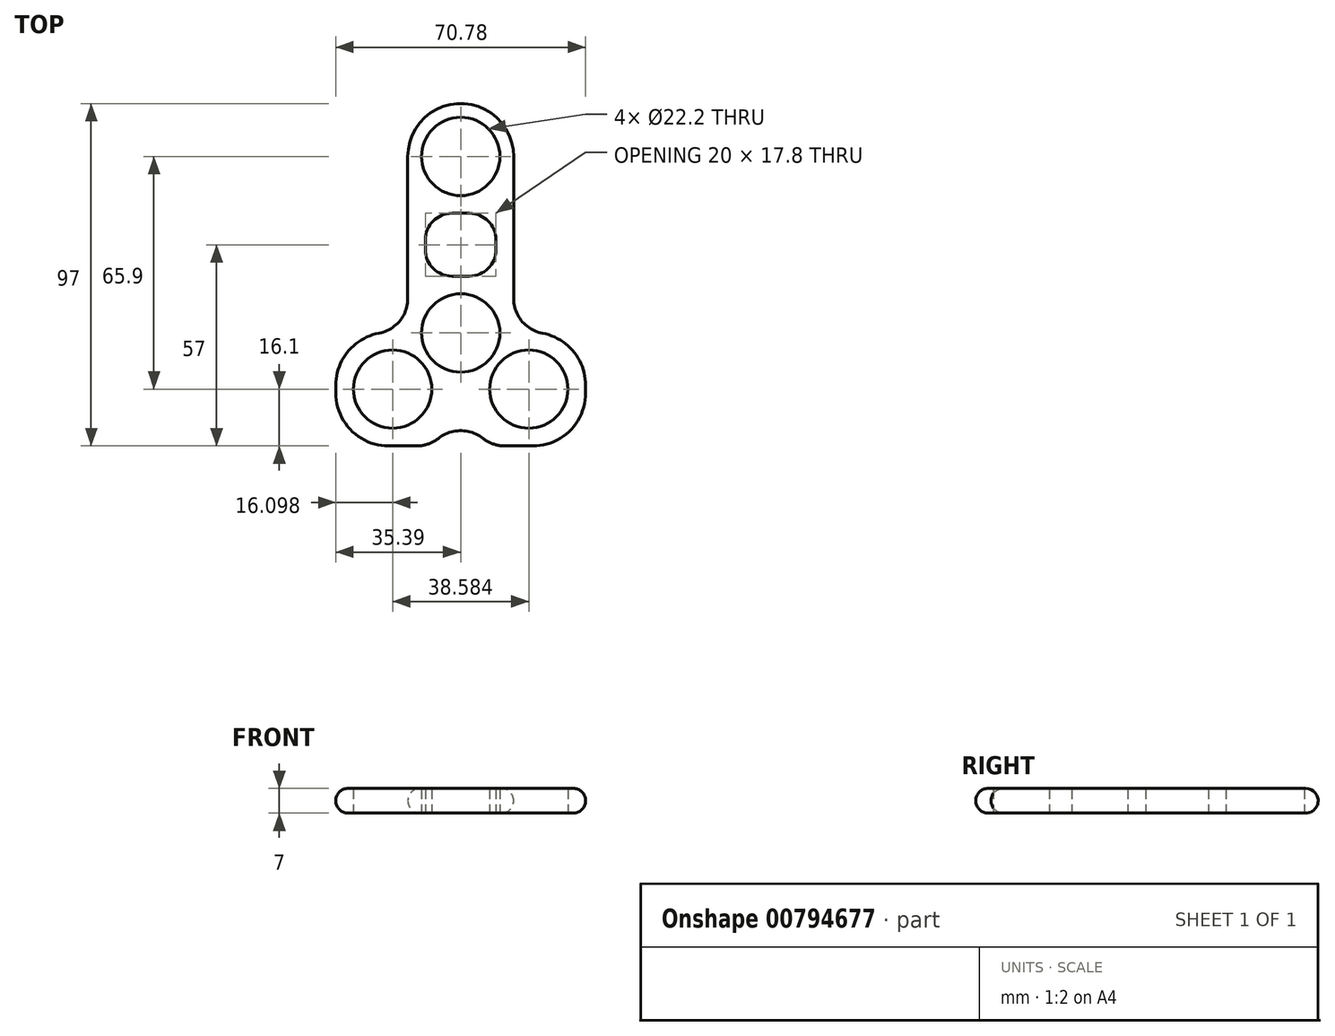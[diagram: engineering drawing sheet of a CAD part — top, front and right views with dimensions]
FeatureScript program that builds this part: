
annotation { "Feature Type Name" : "Feature", "Feature Type Description" : "" }
export const myFeature = defineFeature(function(context is Context, id is Id, definition is map)
    precondition{}
    {
        {
            var Q0;
            Q0=qCreatedBy(makeId("Top.planeOp"),FACE);
            var sketch = newSketch(context, id + "F0", { "sketchPlane" : qUnion([Q0])});
            skCircle(sketch, "E0", {"center": v(0, 50) * mm, "radius": 11.1 * mm});
            skCircle(sketch, "E1", {"center": v(0, 0) * mm, "radius": 11.1 * mm});
            skCircle(sketch, "E2", {"center": v(-19.3, -15.9) * mm, "radius": 11.1 * mm});
            skCircle(sketch, "E3", {"center": v(19.3, -15.9) * mm, "radius": 11.1 * mm});
            skLineSegment(sketch, "E4", {"start": v(-15, 0.2) * mm, "end": v(-15, 60.2) * mm});
            skLineSegment(sketch, "E5", {"start": v(-15, 0.2) * mm, "end": v(-35.4, 0.2) * mm});
            skLineSegment(sketch, "E6", {"start": v(-35.4, 0.2) * mm, "end": v(-35.4, -32) * mm});
            skLineSegment(sketch, "E7", {"start": v(-35.4, -32) * mm, "end": v(0, -32) * mm});
            skLineSegment(sketch, "E8", {"start": v(0, -32) * mm, "end": v(35.4, -32) * mm});
            skLineSegment(sketch, "E9", {"start": v(35.4, -32) * mm, "end": v(35.4, 0.2) * mm});
            skLineSegment(sketch, "E10", {"start": v(35.4, 0.2) * mm, "end": v(15, 0.2) * mm});
            skLineSegment(sketch, "E11", {"start": v(15, 0.2) * mm, "end": v(15, 60.2) * mm});
            skLineSegment(sketch, "E12", {"start": v(15, 60.2) * mm, "end": v(-15, 60.2) * mm});
            skLineSegment(sketch, "E13", {"start": v(-65.85, -15.9) * mm, "end": v(63.66, -15.9) * mm, "construction": true});
            skCircle(sketch, "E14", {"center": v(0, 50) * mm, "radius": 15 * mm});
            skArc(sketch, "E15", {"start": v(8.4, -32) * mm, "mid": v(0, -27.7) * mm, "end": v(-8.4, -32) * mm});
            skLineSegment(sketch, "E16", {"start": v(-10, 33.9) * mm, "end": v(-10, 16.1) * mm});
            skLineSegment(sketch, "E17", {"start": v(-10, 16.1) * mm, "end": v(10, 16.1) * mm});
            skLineSegment(sketch, "E18", {"start": v(10, 16.1) * mm, "end": v(10, 33.9) * mm});
            skLineSegment(sketch, "E19", {"start": v(10, 33.9) * mm, "end": v(-10, 33.9) * mm});
            skSolve(sketch);
        }
        {
            var Q0;
            {var subQ0=sQuery(id+"F0.wireOp",EDGE,"E14");var subQ1=sQuery(id+"F0.wireOp",EDGE,"E12");var subQ2=makeQuery(id+"F0.imprint","INTERSECT",VERTEX,{"disambiguationData":[OD(0.0)],"derivedFrom":[subQ1,subQ0]});Q0=makeQuery(id+"F0.imprint","IMPRINT",FACE,{"disambiguationData":[TD([[makeQuery(id+"F0.imprint","IMPRINT",EDGE,{"disambiguationData":[TD([[subQ2,-1.0]])],"derivedFrom":subQ1}),-1.0]])]});}
            var Q1;
            Q1=makeQuery(id+"F0.imprint","IMPRINT",FACE,{"disambiguationData":[TD([[makeQuery(id+"F0.imprint","IMPRINT",EDGE,{"derivedFrom":sQuery(id+"F0.wireOp",EDGE,"E1")}),-1.0]])]});
            var Q2;
            Q2=makeQuery(id+"F0.imprint","IMPRINT",FACE,{"disambiguationData":[TD([[makeQuery(id+"F0.imprint","IMPRINT",EDGE,{"derivedFrom":sQuery(id+"F0.wireOp",EDGE,"E0")}),-1.0]])]});
            var Q3;
            {var subQ2=sQuery(id+"F0.wireOp",EDGE,"E12");var subQ5=sQuery(id+"F0.wireOp",EDGE,"E0");var subQ7=makeQuery(id+"F0.imprint","INTERSECT",VERTEX,{"disambiguationData":[OD(0.0)],"derivedFrom":[subQ5,subQ2]});Q3=makeQuery(id+"F0.imprint","IMPRINT",FACE,{"disambiguationData":[TD([[makeQuery(id+"F0.imprint","IMPRINT",EDGE,{"disambiguationData":[TD([[subQ7,1.0]])],"derivedFrom":subQ5}),-1.0]])]});}
            extrude(context, id + "F1", {"entities" : qUnion([Q0, Q1, Q2, Q3]), "depth" : 7 * mm, "offsetDistance" : 25 * mm});
        }
        {
            var Q0;
            Q0=makeQuery(id+"F1.opExtrude","SWEPT_EDGE",EDGE,{"disambiguationData":[OSD([sQuery(id+"F0.wireOp",EDGE,"E5"),sQuery(id+"F0.wireOp",EDGE,"E6")])]});
            var Q1;
            Q1=makeQuery(id+"F1.opExtrude","SWEPT_EDGE",EDGE,{"disambiguationData":[OSD([sQuery(id+"F0.wireOp",EDGE,"E6"),sQuery(id+"F0.wireOp",EDGE,"E7")])]});
            var Q2;
            Q2=makeQuery(id+"F1.opExtrude","SWEPT_EDGE",EDGE,{"disambiguationData":[OSD([sQuery(id+"F0.wireOp",EDGE,"E9"),sQuery(id+"F0.wireOp",EDGE,"E10")])]});
            var Q3;
            Q3=makeQuery(id+"F1.opExtrude","SWEPT_EDGE",EDGE,{"disambiguationData":[OSD([sQuery(id+"F0.wireOp",EDGE,"E8"),sQuery(id+"F0.wireOp",EDGE,"E9")])]});
            fillet(context, id + "F2", {"entities" : qUnion([Q0, Q1, Q2, Q3]), "radius" : 15 * mm, "tangentPropagation" : true, "allowEdgeOverflow" : false});
        }
        {
            var Q0;
            Q0=makeQuery(id+"F1.opExtrude","SWEPT_EDGE",EDGE,{"disambiguationData":[OSD([sQuery(id+"F0.wireOp",EDGE,"E7"),sQuery(id+"F0.wireOp",EDGE,"5uxY0wwV-qU5a-CC5X-hWH9-kk7bbz8uba4x")])]});
            var Q1;
            Q1=makeQuery(id+"F1.opExtrude","SWEPT_EDGE",EDGE,{"disambiguationData":[OSD([sQuery(id+"F0.wireOp",EDGE,"E8"),sQuery(id+"F0.wireOp",EDGE,"5uxY0wwV-qU5a-CC5X-hWH9-kk7bbz8uba4x")])]});
            var Q2;
            Q2=makeQuery(id+"F1.opExtrude","SWEPT_EDGE",EDGE,{"disambiguationData":[OSD([sQuery(id+"F0.wireOp",EDGE,"E10"),sQuery(id+"F0.wireOp",EDGE,"E11")])]});
            var Q3;
            Q3=makeQuery(id+"F1.opExtrude","SWEPT_EDGE",EDGE,{"disambiguationData":[OSD([sQuery(id+"F0.wireOp",EDGE,"E4"),sQuery(id+"F0.wireOp",EDGE,"E5")])]});
            fillet(context, id + "F3", {"entities" : qUnion([Q0, Q1, Q2, Q3]), "radius" : 10 * mm, "tangentPropagation" : true, "allowEdgeOverflow" : false});
        }
        {
            var Q0;
            {var subQ0=sQuery(id+"F0.wireOp",EDGE,"E7");var subQ1=sQuery(id+"F0.wireOp",EDGE,"E6");Q0=makeQuery(id+"F2.opFillet","BLEND_EDGE",EDGE,{"blendedFrom":[makeQuery(id+"F1.opExtrude","SWEPT_EDGE",EDGE,{"disambiguationData":[OSD([subQ1,subQ0])]}),makeQuery(id+"F1.opExtrude","CAP_FACE",FACE,{"disambiguationData":[OSD([sQuery(id+"F0.wireOp",EDGE,"E0"),sQuery(id+"F0.wireOp",EDGE,"E1"),sQuery(id+"F0.wireOp",EDGE,"E2"),sQuery(id+"F0.wireOp",EDGE,"E3"),sQuery(id+"F0.wireOp",EDGE,"E4"),sQuery(id+"F0.wireOp",EDGE,"E5"),subQ1,subQ0,sQuery(id+"F0.wireOp",EDGE,"E8"),sQuery(id+"F0.wireOp",EDGE,"E9"),sQuery(id+"F0.wireOp",EDGE,"E10"),sQuery(id+"F0.wireOp",EDGE,"E11"),sQuery(id+"F0.wireOp",EDGE,"E14"),sQuery(id+"F0.wireOp",EDGE,"5uxY0wwV-qU5a-CC5X-hWH9-kk7bbz8uba4x")])],"isStart":false})],"blendedInto":[makeQuery(id+"F1.opExtrude","CAP_FACE",FACE,{"disambiguationData":[OSD([sQuery(id+"F0.wireOp",EDGE,"E0"),sQuery(id+"F0.wireOp",EDGE,"E1"),sQuery(id+"F0.wireOp",EDGE,"E2"),sQuery(id+"F0.wireOp",EDGE,"E3"),sQuery(id+"F0.wireOp",EDGE,"E4"),sQuery(id+"F0.wireOp",EDGE,"E5"),subQ1,subQ0,sQuery(id+"F0.wireOp",EDGE,"E8"),sQuery(id+"F0.wireOp",EDGE,"E9"),sQuery(id+"F0.wireOp",EDGE,"E10"),sQuery(id+"F0.wireOp",EDGE,"E11"),sQuery(id+"F0.wireOp",EDGE,"E14"),sQuery(id+"F0.wireOp",EDGE,"5uxY0wwV-qU5a-CC5X-hWH9-kk7bbz8uba4x")])],"isStart":false})]});}
            var Q1;
            {var subQ0=sQuery(id+"F0.wireOp",EDGE,"E9");var subQ1=sQuery(id+"F0.wireOp",EDGE,"E8");Q1=makeQuery(id+"F2.opFillet","BLEND_EDGE",EDGE,{"blendedFrom":[makeQuery(id+"F1.opExtrude","SWEPT_EDGE",EDGE,{"disambiguationData":[OSD([subQ1,subQ0])]}),makeQuery(id+"F1.opExtrude","CAP_FACE",FACE,{"disambiguationData":[OSD([sQuery(id+"F0.wireOp",EDGE,"E0"),sQuery(id+"F0.wireOp",EDGE,"E1"),sQuery(id+"F0.wireOp",EDGE,"E2"),sQuery(id+"F0.wireOp",EDGE,"E3"),sQuery(id+"F0.wireOp",EDGE,"E4"),sQuery(id+"F0.wireOp",EDGE,"E5"),sQuery(id+"F0.wireOp",EDGE,"E6"),sQuery(id+"F0.wireOp",EDGE,"E7"),subQ1,subQ0,sQuery(id+"F0.wireOp",EDGE,"E10"),sQuery(id+"F0.wireOp",EDGE,"E11"),sQuery(id+"F0.wireOp",EDGE,"E14"),sQuery(id+"F0.wireOp",EDGE,"5uxY0wwV-qU5a-CC5X-hWH9-kk7bbz8uba4x")])],"isStart":true})],"blendedInto":[makeQuery(id+"F1.opExtrude","CAP_FACE",FACE,{"disambiguationData":[OSD([sQuery(id+"F0.wireOp",EDGE,"E0"),sQuery(id+"F0.wireOp",EDGE,"E1"),sQuery(id+"F0.wireOp",EDGE,"E2"),sQuery(id+"F0.wireOp",EDGE,"E3"),sQuery(id+"F0.wireOp",EDGE,"E4"),sQuery(id+"F0.wireOp",EDGE,"E5"),sQuery(id+"F0.wireOp",EDGE,"E6"),sQuery(id+"F0.wireOp",EDGE,"E7"),subQ1,subQ0,sQuery(id+"F0.wireOp",EDGE,"E10"),sQuery(id+"F0.wireOp",EDGE,"E11"),sQuery(id+"F0.wireOp",EDGE,"E14"),sQuery(id+"F0.wireOp",EDGE,"5uxY0wwV-qU5a-CC5X-hWH9-kk7bbz8uba4x")])],"isStart":true})]});}
            fillet(context, id + "F4", {"entities" : qUnion([Q0, Q1]), "radius" : 3.5 * mm, "tangentPropagation" : true, "allowEdgeOverflow" : false});
        }
        {
            var Q0;
            Q0=makeQuery(id+"F1.opExtrude","SWEPT_EDGE",EDGE,{"disambiguationData":[OSD([sQuery(id+"F0.wireOp",EDGE,"E17"),sQuery(id+"F0.wireOp",EDGE,"E18")])]});
            var Q1;
            Q1=makeQuery(id+"F1.opExtrude","SWEPT_EDGE",EDGE,{"disambiguationData":[OSD([sQuery(id+"F0.wireOp",EDGE,"E16"),sQuery(id+"F0.wireOp",EDGE,"E17")])]});
            var Q2;
            Q2=makeQuery(id+"F1.opExtrude","SWEPT_EDGE",EDGE,{"disambiguationData":[OSD([sQuery(id+"F0.wireOp",EDGE,"E18"),sQuery(id+"F0.wireOp",EDGE,"E19")])]});
            var Q3;
            Q3=makeQuery(id+"F1.opExtrude","SWEPT_EDGE",EDGE,{"disambiguationData":[OSD([sQuery(id+"F0.wireOp",EDGE,"E16"),sQuery(id+"F0.wireOp",EDGE,"E19")])]});
            fillet(context, id + "F5", {"entities" : qUnion([Q0, Q1, Q2, Q3]), "radius" : 7.5 * mm, "tangentPropagation" : true, "allowEdgeOverflow" : false});
        }
    });
